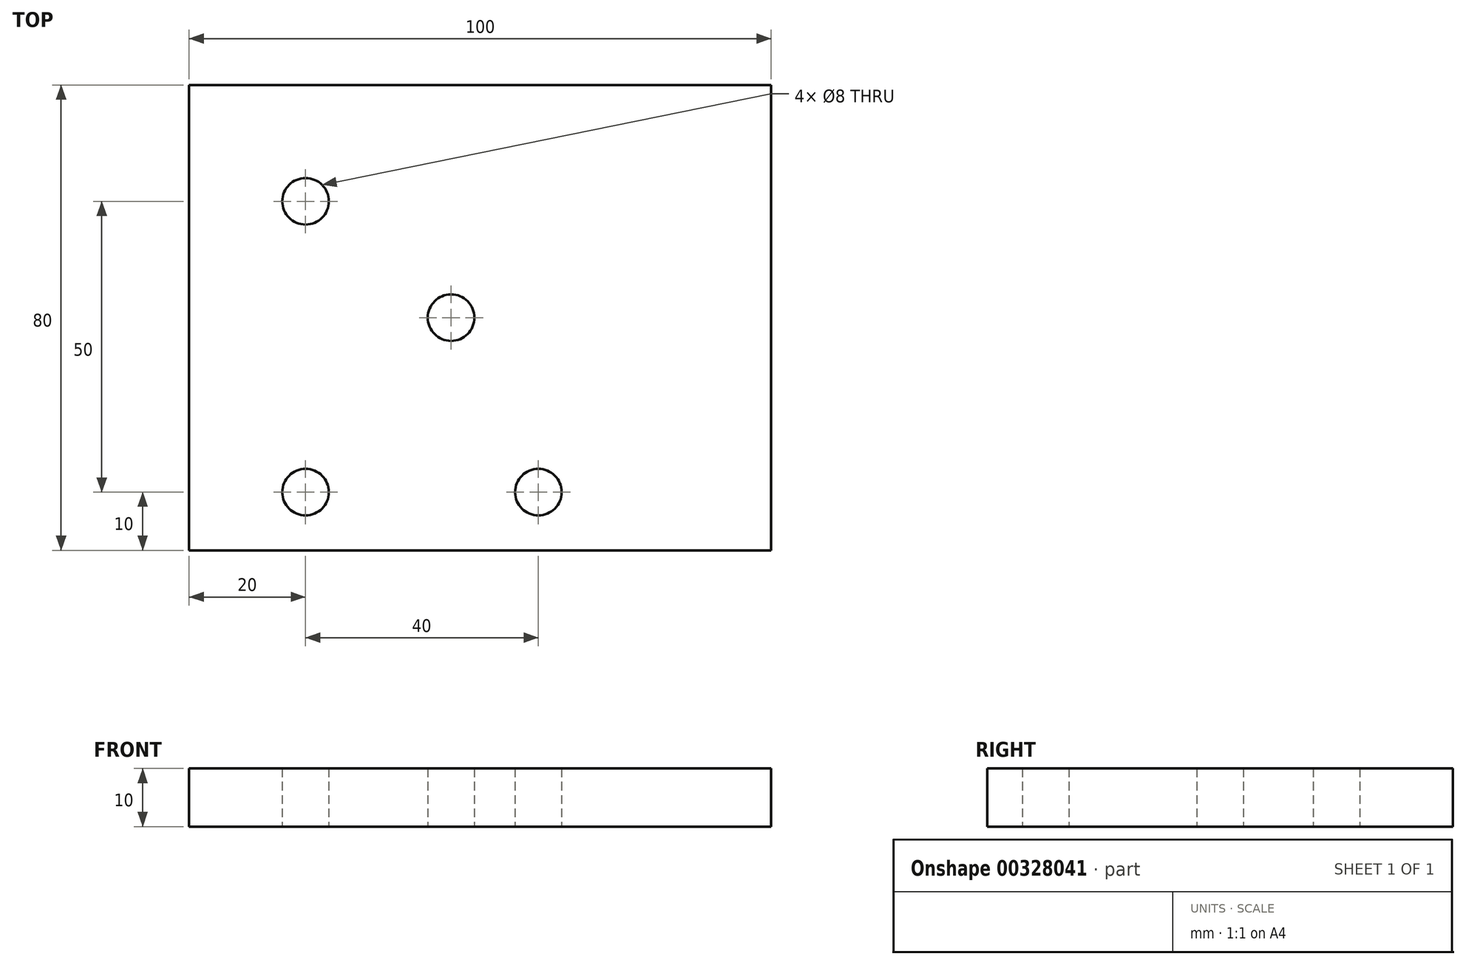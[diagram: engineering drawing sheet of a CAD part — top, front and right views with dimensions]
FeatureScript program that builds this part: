
annotation { "Feature Type Name" : "Feature", "Feature Type Description" : "" }
export const myFeature = defineFeature(function(context is Context, id is Id, definition is map)
    precondition{}
    {
        {
            var Q0;
            Q0=qCreatedBy(makeId("Top.planeOp"),FACE);
            var sketch = newSketch(context, id + "F0", { "sketchPlane" : qUnion([Q0])});
            skLineSegment(sketch, "E0.bottom", {"start": v(0, 80) * mm, "end": v(100, 80) * mm});
            skLineSegment(sketch, "E0.top", {"start": v(0, 0) * mm, "end": v(100, 0) * mm});
            skLineSegment(sketch, "E0.left", {"start": v(0, 80) * mm, "end": v(0, 0) * mm});
            skLineSegment(sketch, "E0.right", {"start": v(100, 80) * mm, "end": v(100, 0) * mm});
            skCircle(sketch, "E1", {"center": v(20, 60) * mm, "radius": 4 * mm});
            skCircle(sketch, "E2", {"center": v(45, 40) * mm, "radius": 4 * mm});
            skCircle(sketch, "E3", {"center": v(20, 10) * mm, "radius": 4 * mm});
            skCircle(sketch, "E4", {"center": v(60, 10) * mm, "radius": 4 * mm});
            skSolve(sketch);
        }
        {
            var Q0;
            Q0=makeQuery(id+"F0.imprint","IMPRINT",FACE,{"disambiguationData":[TD([[makeQuery(id+"F0.imprint","IMPRINT",EDGE,{"derivedFrom":sQuery(id+"F0.wireOp",EDGE,"E0.bottom")}),-1.0]])]});
            extrude(context, id + "F1", {"entities" : qUnion([Q0]), "depth" : 10 * mm});
        }
    });
